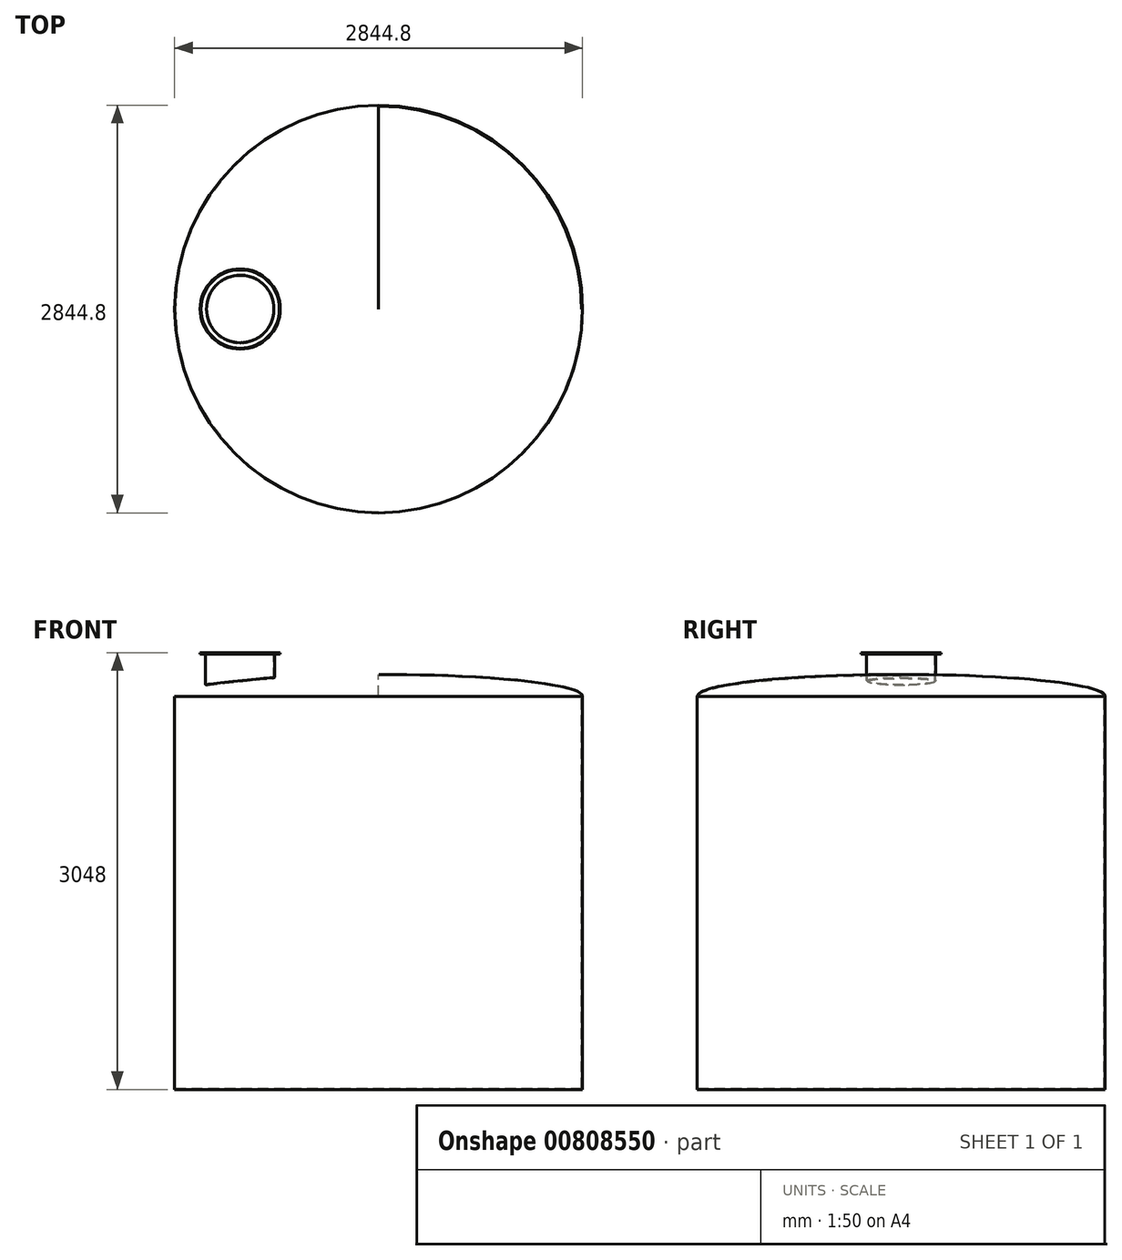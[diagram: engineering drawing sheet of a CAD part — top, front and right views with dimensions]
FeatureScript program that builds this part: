
annotation { "Feature Type Name" : "Feature", "Feature Type Description" : "" }
export const myFeature = defineFeature(function(context is Context, id is Id, definition is map)
    precondition{}
    {
        {
            var Q0;
            Q0=qCreatedBy(makeId("Right.planeOp"),FACE);
            var sketch = newSketch(context, id + "F0", { "sketchPlane" : qUnion([Q0])});
            skLineSegment(sketch, "E0.bottom", {"start": v(0, 0) * mm, "end": v(1422.4, 0) * mm});
            skLineSegment(sketch, "E0.left", {"start": v(0, 0) * mm, "end": v(0, 2743.2) * mm, "construction": true});
            skLineSegment(sketch, "E0.right", {"start": v(1422.4, 0) * mm, "end": v(1422.4, 2743.2) * mm});
            skEllipticalArc(sketch, "E1", {});
            skLineSegment(sketch, "E2", {"start": v(0, 2895.6) * mm, "end": v(0, 0) * mm});
            const initialGuessF0  = {"E1": [0, 2.7432, 1, 0, 1.4224, 0.1524, 6.283185307179585, 1.5707963267948966]};
            skSetInitialGuess(sketch, initialGuessF0);
            skSolve(sketch);
        }
        {
            var Q0;
            Q0 = qSketchRegion(id + "F0", true);
            var Q1;
            Q1=sQuery(id+"F0.wireOp",EDGE,"E2");
            revolve(context, id + "F1", {"surfaceOperationType" : NewSurfaceOperationType.NEW, "entities" : qUnion([Q0]), "axis" : qUnion([Q1]), "revolveType" : RevolveType.FULL});
        }
        {
            var Q0;
            Q0=qCreatedBy(makeId("Top.planeOp"),FACE);
            cPlane(context, id + "F2", {"entities" : qUnion([Q0]), "cplaneType" : CPlaneType.OFFSET, "offset" : 3048 * mm, "width" : 152.4 * mm, "height" : 152.4 * mm});
        }
        {
            var Q0;
            Q0=qCreatedBy(id+"F2.planeOp",FACE);
            var sketch = newSketch(context, id + "F3", { "sketchPlane" : qUnion([Q0])});
            skCircle(sketch, "E3", {"center": v(-965.2, 0) * mm, "radius": 241.3 * mm});
            skCircle(sketch, "E4", {"center": v(-965.2, 0) * mm, "radius": 279.4 * mm});
            skSolve(sketch);
        }
        {
            var Q0;
            Q0=makeQuery(id+"F3.imprint","IMPRINT",FACE,{"disambiguationData":[TD([[makeQuery(id+"F3.imprint","IMPRINT",EDGE,{"derivedFrom":sQuery(id+"F3.wireOp",EDGE,"E3")}),1.0]])]});
            extrude(context, id + "F4", {"entities" : qUnion([Q0]), "operationType" : NewBodyOperationType.ADD, "endBound" : BoundingType.UP_TO_NEXT, "oppositeDirection" : true, "depth" : 25.4 * mm, "offsetDistance" : 25.4 * mm});
        }
        {
            var Q0;
            Q0 = qSketchRegion(id + "F3", true);
            extrude(context, id + "F5", {"entities" : qUnion([Q0]), "operationType" : NewBodyOperationType.ADD, "oppositeDirection" : true, "depth" : 9.52 * mm, "offsetDistance" : 25.4 * mm});
        }
        {
            var Q0;
            {var subQ0=sQuery(id+"F3.wireOp",EDGE,"E3");Q0=makeQuery(id+"F5.boolean.opBoolean","MERGE",FACE,{"derivedFrom":[makeQuery(id+"F4.opExtrude","CAP_FACE",FACE,{"disambiguationData":[OSD([subQ0])],"isStart":true}),makeQuery(id+"F5.opExtrude","CAP_FACE",FACE,{"disambiguationData":[OSD([subQ0,sQuery(id+"F3.wireOp",EDGE,"E4")])],"isStart":true})]});}
            shell(context, id + "F6", {"entities" : qUnion([Q0]), "thickness" : 6.35 * mm});
        }
    });
